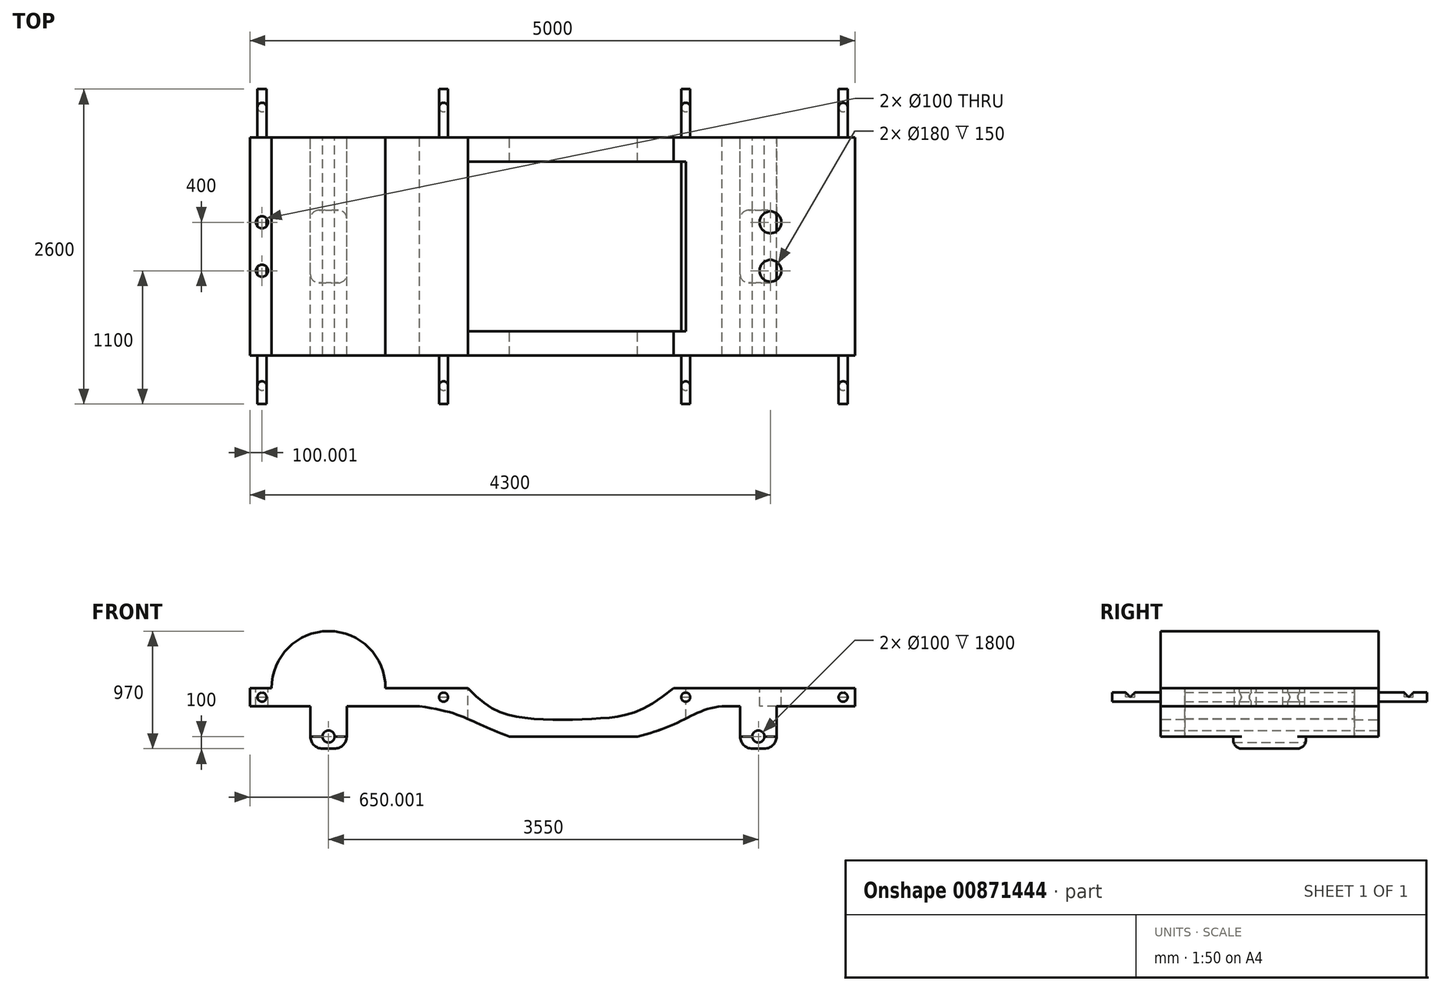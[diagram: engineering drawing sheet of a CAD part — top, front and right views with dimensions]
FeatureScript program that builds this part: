
annotation { "Feature Type Name" : "Feature", "Feature Type Description" : "" }
export const myFeature = defineFeature(function(context is Context, id is Id, definition is map)
    precondition{}
    {
        {
            var Q0;
            Q0=qCreatedBy(makeId("Front.planeOp"),FACE);
            var sketch = newSketch(context, id + "F0", { "sketchPlane" : qUnion([Q0])});
            skLineSegment(sketch, "E0", {"start": v(-2207.1, 0) * mm, "end": v(-2207.1, -150) * mm});
            skLineSegment(sketch, "E1", {"start": v(-2207.1, -150) * mm, "end": v(-807.1, -150) * mm});
            skFitSpline(sketch, "E2", {"points": [v(-807.1, -150) * mm, v(-307.1, -300) * mm, v(192.9, -450) * mm], "startDerivative": vector(1549.63, -206.62) * mm, "endDerivative": vector(1157.34, -66.43) * mm});
            skFitSpline(sketch, "E3", {"points": [v(192.9, -450) * mm, v(692.9, -450) * mm, v(1292.9, -300) * mm, v(1692.9, -150) * mm], "startDerivative": vector(931.79, -77.59) * mm, "endDerivative": vector(1482.21, 107.32) * mm});
            skLineSegment(sketch, "E4", {"start": v(1692.9, -150) * mm, "end": v(2792.9, -150) * mm});
            skLineSegment(sketch, "E5", {"start": v(2792.9, -150) * mm, "end": v(2792.9, 0) * mm});
            skLineSegment(sketch, "E6", {"start": v(-2207.1, 0) * mm, "end": v(-407.1, 0) * mm});
            skFitSpline(sketch, "E7", {"points": [v(-407.1, 0) * mm, v(92.9, -250) * mm, v(693, -250) * mm, v(1293, 0) * mm], "startDerivative": vector(1561.36, -1754.44) * mm, "endDerivative": vector(2212.71, 1856.89) * mm});
            skLineSegment(sketch, "E8", {"start": v(1293, 0) * mm, "end": v(2792.9, 0) * mm});
            skSolve(sketch);
        }
        {
            var Q0;
            Q0=qSketchRegion(id+"F0",true);
            extrude(context, id + "F1", {"entities" : qUnion([Q0]), "depth" : 1800 * mm});
        }
        {
            var Q0;
            Q0=qCreatedBy(makeId("Top.planeOp"),FACE);
            var sketch = newSketch(context, id + "F2", { "sketchPlane" : qUnion([Q0])});
            skLineSegment(sketch, "E9.bottom", {"start": v(-407.1, -200) * mm, "end": v(1392.9, -200) * mm});
            skLineSegment(sketch, "E9.top", {"start": v(-407.1, -1600) * mm, "end": v(1392.9, -1600) * mm});
            skLineSegment(sketch, "E9.left", {"start": v(-407.1, -200) * mm, "end": v(-407.1, -1600) * mm});
            skLineSegment(sketch, "E9.right", {"start": v(1392.9, -200) * mm, "end": v(1392.9, -1600) * mm});
            skCircle(sketch, "E10", {"center": v(2092.9, -700) * mm, "radius": 90 * mm});
            skCircle(sketch, "E11", {"center": v(2092.9, -1100) * mm, "radius": 90 * mm});
            skCircle(sketch, "E12", {"center": v(-2107.1, -700) * mm, "radius": 50 * mm});
            skCircle(sketch, "E13", {"center": v(-2107.1, -1100) * mm, "radius": 50 * mm});
            skLineSegment(sketch, "E14", {"start": v(-2433.44, -900) * mm, "end": v(3216.39, -900) * mm, "construction": true});
            skSolve(sketch);
        }
        {
            var Q0;
            Q0=makeQuery(id+"F2.imprint","IMPRINT",FACE,{"disambiguationData":[TD([[makeQuery(id+"F2.imprint","IMPRINT",EDGE,{"derivedFrom":sQuery(id+"F2.wireOp",EDGE,"2RptNs6A-mePP-rphL-eACh-eVUUGwHWJbpe.bottom")}),-1.0]])]});
            var Q1;
            Q1=makeQuery(id+"F2.imprint","IMPRINT",FACE,{"disambiguationData":[TD([[makeQuery(id+"F2.imprint","IMPRINT",EDGE,{"derivedFrom":sQuery(id+"F2.wireOp",EDGE,"E9.bottom")}),-1.0]])]});
            var Q2;
            Q2=makeQuery(id+"F2.imprint","IMPRINT",FACE,{"disambiguationData":[TD([[makeQuery(id+"F2.imprint","IMPRINT",EDGE,{"derivedFrom":sQuery(id+"F2.wireOp",EDGE,"kMBfGQrs-vHd1-vmnO-5CYD-BuNOrFmh5Xz2.bottom")}),1.0]])]});
            var Q3;
            Q3=makeQuery(id+"F2.imprint","IMPRINT",FACE,{"disambiguationData":[TD([[makeQuery(id+"F2.imprint","IMPRINT",EDGE,{"derivedFrom":sQuery(id+"F2.wireOp",EDGE,"E11")}),1.0]])]});
            var Q4;
            Q4=makeQuery(id+"F2.imprint","IMPRINT",FACE,{"disambiguationData":[TD([[makeQuery(id+"F2.imprint","IMPRINT",EDGE,{"derivedFrom":sQuery(id+"F2.wireOp",EDGE,"E10")}),1.0]])]});
            var Q5;
            Q5=makeQuery(id+"F2.imprint","IMPRINT",FACE,{"disambiguationData":[TD([[makeQuery(id+"F2.imprint","IMPRINT",EDGE,{"derivedFrom":sQuery(id+"F2.wireOp",EDGE,"E12")}),1.0]])]});
            var Q6;
            Q6=makeQuery(id+"F2.imprint","IMPRINT",FACE,{"disambiguationData":[TD([[makeQuery(id+"F2.imprint","IMPRINT",EDGE,{"derivedFrom":sQuery(id+"F2.wireOp",EDGE,"E13")}),1.0]])]});
            extrude(context, id + "F3", {"entities" : qUnion([Q0, Q1, Q2, Q3, Q4, Q5, Q6]), "operationType" : NewBodyOperationType.REMOVE, "oppositeDirection" : true, "depth" : 1000 * mm, "hasSecondDirection" : true, "secondDirectionOppositeDirection" : false, "secondDirectionDepth" : 680 * mm});
        }
        {
            var Q0;
            Q0=makeQuery(id+"F2.imprint","IMPRINT",FACE,{"disambiguationData":[TD([[makeQuery(id+"F2.imprint","IMPRINT",EDGE,{"derivedFrom":sQuery(id+"F2.wireOp",EDGE,"E9.bottom")}),-1.0]])]});
            extrude(context, id + "F4", {"entities" : qUnion([Q0]), "operationType" : NewBodyOperationType.REMOVE, "depth" : 25 * mm});
        }
        {
            var Q0;
            Q0=qCreatedBy(makeId("Front.planeOp"),FACE);
            var sketch = newSketch(context, id + "F5", { "sketchPlane" : qUnion([Q0])});
            skLineSegment(sketch, "E15.bottom", {"start": v(1842.9, -150) * mm, "end": v(2142.9, -150) * mm});
            skLineSegment(sketch, "E15.top", {"start": v(1842.9, -500) * mm, "end": v(2142.9, -500) * mm});
            skLineSegment(sketch, "E15.left", {"start": v(1842.9, -150) * mm, "end": v(1842.9, -500) * mm});
            skLineSegment(sketch, "E15.right", {"start": v(2142.9, -150) * mm, "end": v(2142.9, -500) * mm});
            skLineSegment(sketch, "E16.bottom", {"start": v(-1707.1, -150) * mm, "end": v(-1407.1, -150) * mm});
            skLineSegment(sketch, "E16.top", {"start": v(-1707.1, -500) * mm, "end": v(-1407.1, -500) * mm});
            skLineSegment(sketch, "E16.left", {"start": v(-1707.1, -150) * mm, "end": v(-1707.1, -500) * mm});
            skLineSegment(sketch, "E16.right", {"start": v(-1407.1, -150) * mm, "end": v(-1407.1, -500) * mm});
            skCircle(sketch, "E17", {"center": v(-1557.1, -400) * mm, "radius": 50 * mm});
            skCircle(sketch, "E18", {"center": v(1992.9, -400) * mm, "radius": 50 * mm});
            skSolve(sketch);
        }
        {
            var Q0;
            Q0=makeQuery(id+"F5.imprint","IMPRINT",FACE,{"disambiguationData":[TD([[makeQuery(id+"F5.imprint","IMPRINT",EDGE,{"derivedFrom":sQuery(id+"F5.wireOp",EDGE,"E15.bottom")}),-1.0]])]});
            var Q1;
            Q1=makeQuery(id+"F5.imprint","IMPRINT",FACE,{"disambiguationData":[TD([[makeQuery(id+"F5.imprint","IMPRINT",EDGE,{"derivedFrom":sQuery(id+"F5.wireOp",EDGE,"E16.bottom")}),-1.0]])]});
            extrude(context, id + "F6", {"entities" : qUnion([Q0, Q1]), "operationType" : NewBodyOperationType.ADD, "depth" : 1800 * mm});
        }
        {
            var Q0;
            Q0=makeQuery(id+"F6.opExtrude","SWEPT_EDGE",EDGE,{"disambiguationData":[OSD([sQuery(id+"F5.wireOp",EDGE,"E16.top"),sQuery(id+"F5.wireOp",EDGE,"E16.left")])]});
            var Q1;
            Q1=makeQuery(id+"F6.opExtrude","SWEPT_EDGE",EDGE,{"disambiguationData":[OSD([sQuery(id+"F5.wireOp",EDGE,"E16.top"),sQuery(id+"F5.wireOp",EDGE,"E16.right")])]});
            var Q2;
            Q2=makeQuery(id+"F6.opExtrude","SWEPT_EDGE",EDGE,{"disambiguationData":[OSD([sQuery(id+"F5.wireOp",EDGE,"E15.top"),sQuery(id+"F5.wireOp",EDGE,"E15.left")])]});
            var Q3;
            Q3=makeQuery(id+"F6.opExtrude","SWEPT_EDGE",EDGE,{"disambiguationData":[OSD([sQuery(id+"F5.wireOp",EDGE,"E15.top"),sQuery(id+"F5.wireOp",EDGE,"E15.right")])]});
            fillet(context, id + "F7", {"entities" : qUnion([Q0, Q1, Q2, Q3]), "radius" : 100 * mm, "tangentPropagation" : true, "allowEdgeOverflow" : false});
        }
        {
            var Q0;
            Q0=makeQuery(id+"F6.opExtrude","SWEPT_FACE",FACE,{"disambiguationData":[OSD([sQuery(id+"F5.wireOp",EDGE,"E16.left")])]});
            var sketch = newSketch(context, id + "F8", { "sketchPlane" : qUnion([Q0])});
            skLineSegment(sketch, "E19.bottom", {"start": v(0, -550) * mm, "end": v(600, -550) * mm});
            skLineSegment(sketch, "E19.top", {"start": v(0, -400) * mm, "end": v(600, -400) * mm});
            skLineSegment(sketch, "E19.left", {"start": v(0, -550) * mm, "end": v(0, -400) * mm});
            skLineSegment(sketch, "E19.right", {"start": v(600, -550) * mm, "end": v(600, -400) * mm});
            skLineSegment(sketch, "E20.bottom", {"start": v(1200, -550) * mm, "end": v(1800, -550) * mm});
            skLineSegment(sketch, "E20.top", {"start": v(1200, -400) * mm, "end": v(1800, -400) * mm});
            skLineSegment(sketch, "E20.left", {"start": v(1200, -550) * mm, "end": v(1200, -400) * mm});
            skLineSegment(sketch, "E20.right", {"start": v(1800, -550) * mm, "end": v(1800, -400) * mm});
            skSolve(sketch);
        }
        {
            var Q0;
            {var subQ0=sQuery(id+"F8.wireOp",EDGE,"E20.bottom");Q0=makeQuery(id+"F8.imprint","IMPRINT",FACE,{"disambiguationData":[TD([[makeQuery(id+"F8.imprint","IMPRINT",EDGE,{"derivedFrom":subQ0}),1.0]])]});}
            var Q1;
            {var subQ0=sQuery(id+"F8.wireOp",EDGE,"E20.top");Q1=makeQuery(id+"F8.imprint","IMPRINT",FACE,{"disambiguationData":[TD([[makeQuery(id+"F8.imprint","IMPRINT",EDGE,{"derivedFrom":subQ0}),-1.0]])]});}
            var Q2;
            {var subQ0=sQuery(id+"F8.wireOp",EDGE,"E19.top");Q2=makeQuery(id+"F8.imprint","IMPRINT",FACE,{"disambiguationData":[TD([[makeQuery(id+"F8.imprint","IMPRINT",EDGE,{"derivedFrom":subQ0}),-1.0]])]});}
            var Q3;
            {var subQ0=sQuery(id+"F8.wireOp",EDGE,"E19.bottom");Q3=makeQuery(id+"F8.imprint","IMPRINT",FACE,{"disambiguationData":[TD([[makeQuery(id+"F8.imprint","IMPRINT",EDGE,{"derivedFrom":subQ0}),1.0]])]});}
            extrude(context, id + "F9", {"entities" : qUnion([Q0, Q1, Q2, Q3]), "operationType" : NewBodyOperationType.REMOVE, "oppositeDirection" : true, "depth" : 4000 * mm});
        }
        {
            var Q0;
            {var subQ0=sQuery(id+"F5.wireOp",EDGE,"E15.top");var subQ1=sQuery(id+"F8.wireOp",EDGE,"E19.right");Q0=makeQuery(id+"F9.boolean.opBoolean","COPY",EDGE,{"disambiguationData":[TD([makeQuery(id+"F6.opExtrude","SWEPT_FACE",FACE,{"disambiguationData":[OSD([subQ0])]})])],"derivedFrom":makeQuery(id+"F9.opExtrude","SWEPT_EDGE",EDGE,{"disambiguationData":[OSD([sQuery(id+"F8.wireOp",EDGE,"E19.bottom"),subQ1])]})});}
            var Q1;
            Q1=makeQuery(id+"F9.boolean.opBoolean","INTERSECT",EDGE,{"derivedFrom":[makeQuery(id+"F7.opFillet","BLEND_FACE",FACE,{"disambiguationData":[OSD([sQuery(id+"F5.wireOp",EDGE,"E15.top"),sQuery(id+"F5.wireOp",EDGE,"E15.right")])]}),makeQuery(id+"F9.opExtrude","SWEPT_FACE",FACE,{"disambiguationData":[OSD([sQuery(id+"F8.wireOp",EDGE,"E19.right")])]})]});
            var Q2;
            Q2=makeQuery(id+"F9.boolean.opBoolean","INTERSECT",EDGE,{"derivedFrom":[makeQuery(id+"F7.opFillet","BLEND_FACE",FACE,{"disambiguationData":[OSD([sQuery(id+"F5.wireOp",EDGE,"E15.top"),sQuery(id+"F5.wireOp",EDGE,"E15.right")])]}),makeQuery(id+"F9.opExtrude","SWEPT_FACE",FACE,{"disambiguationData":[OSD([sQuery(id+"F8.wireOp",EDGE,"E20.left")])]})]});
            var Q3;
            Q3=makeQuery(id+"F9.boolean.opBoolean","INTERSECT",EDGE,{"derivedFrom":[makeQuery(id+"F7.opFillet","BLEND_FACE",FACE,{"disambiguationData":[OSD([sQuery(id+"F5.wireOp",EDGE,"E16.top"),sQuery(id+"F5.wireOp",EDGE,"E16.left")])]}),makeQuery(id+"F9.opExtrude","SWEPT_FACE",FACE,{"disambiguationData":[OSD([sQuery(id+"F8.wireOp",EDGE,"E19.right")])]})]});
            var Q4;
            Q4=makeQuery(id+"F9.boolean.opBoolean","INTERSECT",EDGE,{"derivedFrom":[makeQuery(id+"F7.opFillet","BLEND_FACE",FACE,{"disambiguationData":[OSD([sQuery(id+"F5.wireOp",EDGE,"E16.top"),sQuery(id+"F5.wireOp",EDGE,"E16.left")])]}),makeQuery(id+"F9.opExtrude","SWEPT_FACE",FACE,{"disambiguationData":[OSD([sQuery(id+"F8.wireOp",EDGE,"E20.left")])]})]});
            fillet(context, id + "F10", {"entities" : qUnion([Q0, Q1, Q2, Q3, Q4]), "radius" : 70 * mm, "tangentPropagation" : true, "allowEdgeOverflow" : false});
        }
        {
            var Q0;
            Q0=makeQuery(id+"F6.boolean.opBoolean","MERGE",FACE,{"derivedFrom":[makeQuery(id+"F1.opExtrude","CAP_FACE",FACE,{"disambiguationData":[OSD([sQuery(id+"F0.wireOp",EDGE,"E0"),sQuery(id+"F0.wireOp",EDGE,"E1"),sQuery(id+"F0.wireOp",EDGE,"E2"),sQuery(id+"F0.wireOp",EDGE,"E3"),sQuery(id+"F0.wireOp",EDGE,"E4"),sQuery(id+"F0.wireOp",EDGE,"E5"),sQuery(id+"F0.wireOp",EDGE,"E6"),sQuery(id+"F0.wireOp",EDGE,"E7"),sQuery(id+"F0.wireOp",EDGE,"E8")])],"isStart":false}),makeQuery(id+"F6.opExtrude","CAP_FACE",FACE,{"disambiguationData":[OSD([sQuery(id+"F5.wireOp",EDGE,"E15.bottom"),sQuery(id+"F5.wireOp",EDGE,"E15.top"),sQuery(id+"F5.wireOp",EDGE,"E15.left"),sQuery(id+"F5.wireOp",EDGE,"E15.right"),sQuery(id+"F5.wireOp",EDGE,"E18")])],"isStart":false}),makeQuery(id+"F6.opExtrude","CAP_FACE",FACE,{"disambiguationData":[OSD([sQuery(id+"F5.wireOp",EDGE,"E16.bottom"),sQuery(id+"F5.wireOp",EDGE,"E16.top"),sQuery(id+"F5.wireOp",EDGE,"E16.left"),sQuery(id+"F5.wireOp",EDGE,"E16.right"),sQuery(id+"F5.wireOp",EDGE,"E17")])],"isStart":false})]});
            var sketch = newSketch(context, id + "F11", { "sketchPlane" : qUnion([Q0])});
            skArc(sketch, "E21", {"start": v(-1089.78, -50) * mm, "mid": v(-1557.1, 470) * mm, "end": v(-2024.44, -50) * mm});
            skLineSegment(sketch, "E22", {"start": v(-2024.44, -50) * mm, "end": v(-1089.78, -50) * mm});
            skSolve(sketch);
        }
        {
            var Q0;
            Q0=makeQuery(id+"F11.imprint","IMPRINT",FACE,{"disambiguationData":[TD([[makeQuery(id+"F11.imprint","IMPRINT",EDGE,{"derivedFrom":sQuery(id+"F11.wireOp",EDGE,"E21")}),1.0]])]});
            var Q1;
            {var subQ0=sQuery(id+"F11.wireOp",EDGE,"E21");var subQ1=makeQuery(id+"F1.opExtrude","CAP_EDGE",EDGE,{"disambiguationData":[OSD([sQuery(id+"F0.wireOp",EDGE,"E6")])],"isStart":false});var subQ2=makeQuery(id+"F11.imprint","INTERSECT",VERTEX,{"disambiguationData":[OD(0.0)],"derivedFrom":[subQ1,subQ0]});Q1=makeQuery(id+"F11.imprint","IMPRINT",FACE,{"disambiguationData":[TD([[makeQuery(id+"F11.imprint","IMPRINT",EDGE,{"disambiguationData":[TD([[subQ2,-1.0]])],"derivedFrom":subQ0}),1.0]])]});}
            extrude(context, id + "F12", {"entities" : qUnion([Q0, Q1]), "operationType" : NewBodyOperationType.ADD, "oppositeDirection" : true, "depth" : 1800 * mm});
        }
        {
            var Q0;
            Q0=makeQuery(id+"F12.boolean.opBoolean","MERGE",FACE,{"derivedFrom":[makeQuery(id+"F6.boolean.opBoolean","MERGE",FACE,{"derivedFrom":[makeQuery(id+"F1.opExtrude","CAP_FACE",FACE,{"disambiguationData":[OSD([sQuery(id+"F0.wireOp",EDGE,"E0"),sQuery(id+"F0.wireOp",EDGE,"E1"),sQuery(id+"F0.wireOp",EDGE,"E2"),sQuery(id+"F0.wireOp",EDGE,"E3"),sQuery(id+"F0.wireOp",EDGE,"E4"),sQuery(id+"F0.wireOp",EDGE,"E5"),sQuery(id+"F0.wireOp",EDGE,"E6"),sQuery(id+"F0.wireOp",EDGE,"E7"),sQuery(id+"F0.wireOp",EDGE,"E8")])],"isStart":false}),makeQuery(id+"F6.opExtrude","CAP_FACE",FACE,{"disambiguationData":[OSD([sQuery(id+"F5.wireOp",EDGE,"E15.bottom"),sQuery(id+"F5.wireOp",EDGE,"E15.top"),sQuery(id+"F5.wireOp",EDGE,"E15.left"),sQuery(id+"F5.wireOp",EDGE,"E15.right"),sQuery(id+"F5.wireOp",EDGE,"E18")])],"isStart":false}),makeQuery(id+"F6.opExtrude","CAP_FACE",FACE,{"disambiguationData":[OSD([sQuery(id+"F5.wireOp",EDGE,"E16.bottom"),sQuery(id+"F5.wireOp",EDGE,"E16.top"),sQuery(id+"F5.wireOp",EDGE,"E16.left"),sQuery(id+"F5.wireOp",EDGE,"E16.right"),sQuery(id+"F5.wireOp",EDGE,"E17")])],"isStart":false})]}),makeQuery(id+"F12.opExtrude","CAP_FACE",FACE,{"disambiguationData":[OSD([sQuery(id+"F11.wireOp",EDGE,"E21"),sQuery(id+"F11.wireOp",EDGE,"E22")])],"isStart":true})]});
            var sketch = newSketch(context, id + "F13", { "sketchPlane" : qUnion([Q0])});
            skCircle(sketch, "E23", {"center": v(-2107.1, -75) * mm, "radius": 37.5 * mm});
            skCircle(sketch, "E24", {"center": v(-607.1, -75) * mm, "radius": 37.5 * mm});
            skCircle(sketch, "E25", {"center": v(2692.9, -75) * mm, "radius": 37.5 * mm});
            skCircle(sketch, "E26", {"center": v(1392.9, -75) * mm, "radius": 37.5 * mm});
            skSolve(sketch);
        }
        {
            var Q0;
            Q0=makeQuery(id+"F13.imprint","IMPRINT",FACE,{"disambiguationData":[TD([[makeQuery(id+"F13.imprint","IMPRINT",EDGE,{"derivedFrom":sQuery(id+"F13.wireOp",EDGE,"E23")}),1.0]])]});
            var Q1;
            Q1=makeQuery(id+"F13.imprint","IMPRINT",FACE,{"disambiguationData":[TD([[makeQuery(id+"F13.imprint","IMPRINT",EDGE,{"derivedFrom":sQuery(id+"F13.wireOp",EDGE,"E24")}),1.0]])]});
            var Q2;
            Q2=makeQuery(id+"F13.imprint","IMPRINT",FACE,{"disambiguationData":[TD([[makeQuery(id+"F13.imprint","IMPRINT",EDGE,{"derivedFrom":sQuery(id+"F13.wireOp",EDGE,"E26")}),1.0]])]});
            var Q3;
            Q3=makeQuery(id+"F13.imprint","IMPRINT",FACE,{"disambiguationData":[TD([[makeQuery(id+"F13.imprint","IMPRINT",EDGE,{"derivedFrom":sQuery(id+"F13.wireOp",EDGE,"E25")}),1.0]])]});
            extrude(context, id + "F14", {"entities" : qUnion([Q0, Q1, Q2, Q3]), "operationType" : NewBodyOperationType.ADD, "depth" : 400 * mm, "hasSecondDirection" : true, "secondDirectionOppositeDirection" : true, "secondDirectionDepth" : 2200 * mm});
        }
        {
            var Q0;
            Q0=qCreatedBy(makeId("Top.planeOp"),FACE);
            var sketch = newSketch(context, id + "F15", { "sketchPlane" : qUnion([Q0])});
            skCircle(sketch, "E27", {"center": v(-2107.1, -2050) * mm, "radius": 37.5 * mm});
            skCircle(sketch, "E28", {"center": v(-2107.1, 250) * mm, "radius": 37.5 * mm});
            skLineSegment(sketch, "E29", {"start": v(-2107.1, -2429.92) * mm, "end": v(-2107.1, 1499.1) * mm, "construction": true});
            skLineSegment(sketch, "E30", {"start": v(-607.1, -2303.55) * mm, "end": v(-607.1, 1372.73) * mm, "construction": true});
            skCircle(sketch, "E31", {"center": v(-607.1, -2050) * mm, "radius": 37.5 * mm});
            skCircle(sketch, "E32", {"center": v(-607.1, 250) * mm, "radius": 37.5 * mm});
            skLineSegment(sketch, "E33", {"start": v(1392.9, 663.92) * mm, "end": v(1392.9, -2150.45) * mm, "construction": true});
            skLineSegment(sketch, "E34", {"start": v(2692.9, -2329.14) * mm, "end": v(2692.9, 858.87) * mm, "construction": true});
            skCircle(sketch, "E35", {"center": v(1392.9, 250) * mm, "radius": 37.5 * mm});
            skCircle(sketch, "E36", {"center": v(2692.9, 250) * mm, "radius": 37.5 * mm});
            skCircle(sketch, "E37", {"center": v(1392.9, -2050) * mm, "radius": 37.5 * mm});
            skCircle(sketch, "E38", {"center": v(2692.9, -2050) * mm, "radius": 37.5 * mm});
            skSolve(sketch);
        }
        {
            var Q0;
            Q0=makeQuery(id+"F15.imprint","IMPRINT",FACE,{"disambiguationData":[TD([[makeQuery(id+"F15.imprint","IMPRINT",EDGE,{"derivedFrom":sQuery(id+"F15.wireOp",EDGE,"E27")}),1.0]])]});
            var Q1;
            Q1=makeQuery(id+"F15.imprint","IMPRINT",FACE,{"disambiguationData":[TD([[makeQuery(id+"F15.imprint","IMPRINT",EDGE,{"derivedFrom":sQuery(id+"F15.wireOp",EDGE,"E28")}),1.0]])]});
            var Q2;
            Q2=makeQuery(id+"F15.imprint","IMPRINT",FACE,{"disambiguationData":[TD([[makeQuery(id+"F15.imprint","IMPRINT",EDGE,{"derivedFrom":sQuery(id+"F15.wireOp",EDGE,"E31")}),1.0]])]});
            var Q3;
            Q3=makeQuery(id+"F15.imprint","IMPRINT",FACE,{"disambiguationData":[TD([[makeQuery(id+"F15.imprint","IMPRINT",EDGE,{"derivedFrom":sQuery(id+"F15.wireOp",EDGE,"E32")}),1.0]])]});
            var Q4;
            Q4=makeQuery(id+"F15.imprint","IMPRINT",FACE,{"disambiguationData":[TD([[makeQuery(id+"F15.imprint","IMPRINT",EDGE,{"derivedFrom":sQuery(id+"F15.wireOp",EDGE,"E36")}),1.0]])]});
            var Q5;
            Q5=makeQuery(id+"F15.imprint","IMPRINT",FACE,{"disambiguationData":[TD([[makeQuery(id+"F15.imprint","IMPRINT",EDGE,{"derivedFrom":sQuery(id+"F15.wireOp",EDGE,"E37")}),1.0]])]});
            var Q6;
            Q6=makeQuery(id+"F15.imprint","IMPRINT",FACE,{"disambiguationData":[TD([[makeQuery(id+"F15.imprint","IMPRINT",EDGE,{"derivedFrom":sQuery(id+"F15.wireOp",EDGE,"E38")}),1.0]])]});
            var Q7;
            Q7=makeQuery(id+"F15.imprint","IMPRINT",FACE,{"disambiguationData":[TD([[makeQuery(id+"F15.imprint","IMPRINT",EDGE,{"derivedFrom":sQuery(id+"F15.wireOp",EDGE,"E35")}),1.0]])]});
            extrude(context, id + "F16", {"entities" : qUnion([Q0, Q1, Q2, Q3, Q4, Q5, Q6, Q7]), "operationType" : NewBodyOperationType.REMOVE, "oppositeDirection" : true, "depth" : 75 * mm});
        }
    });
